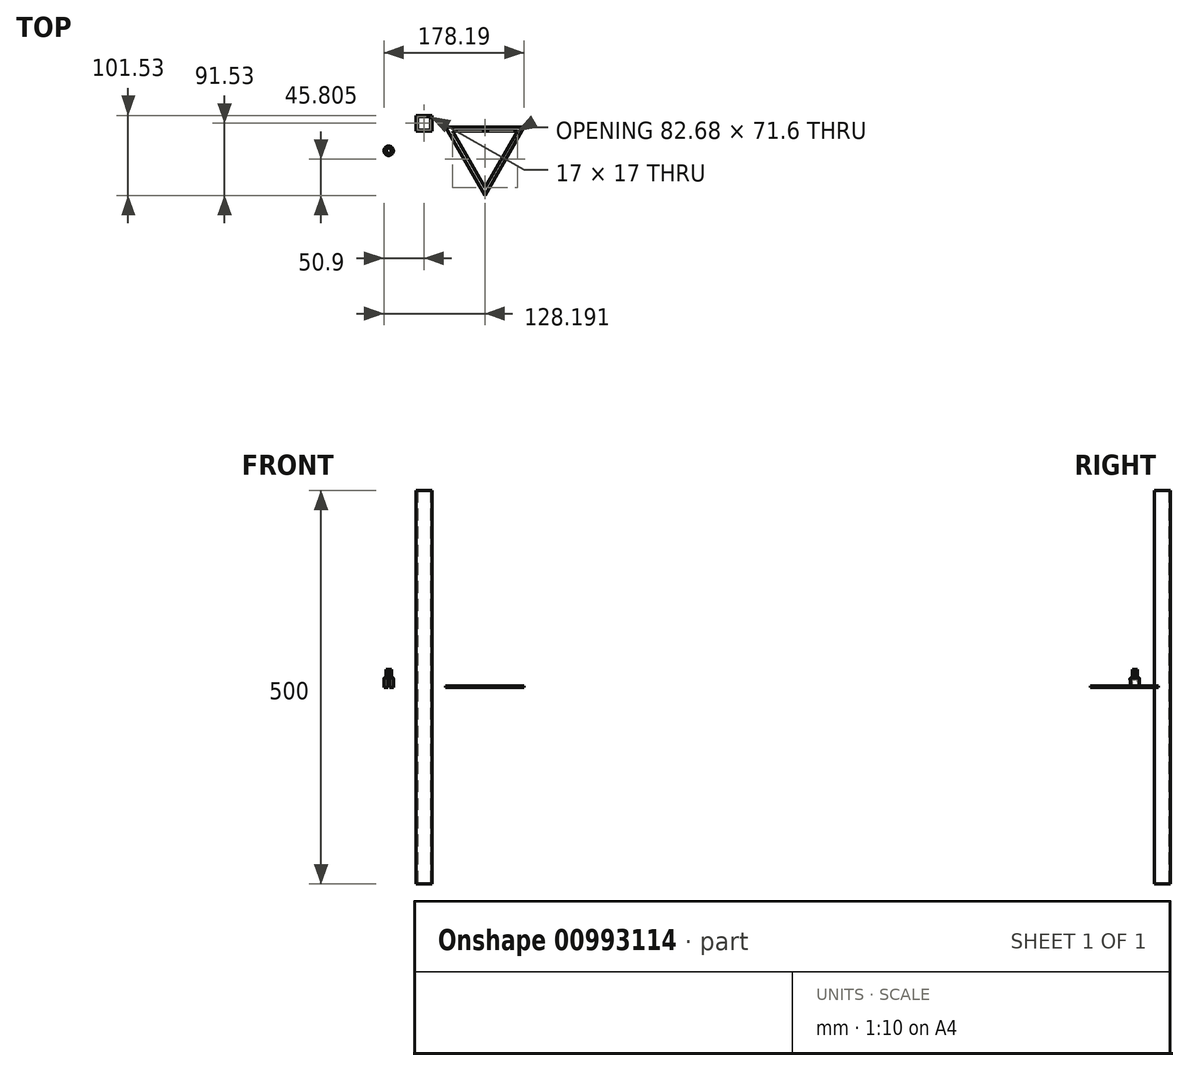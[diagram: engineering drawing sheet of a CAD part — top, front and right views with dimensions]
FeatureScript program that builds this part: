
annotation { "Feature Type Name" : "Feature", "Feature Type Description" : "" }
export const myFeature = defineFeature(function(context is Context, id is Id, definition is map)
    precondition{}
    {
        {
            var Q0;
            Q0=qCreatedBy(makeId("Top.planeOp"),FACE);
            var sketch = newSketch(context, id + "F0", { "sketchPlane" : qUnion([Q0])});
            skLineSegment(sketch, "E0.bottom", {"start": v(-10, 10) * mm, "end": v(10, 10) * mm});
            skLineSegment(sketch, "E0.top", {"start": v(-10, -10) * mm, "end": v(10, -10) * mm});
            skLineSegment(sketch, "E0.left", {"start": v(-10, 10) * mm, "end": v(-10, -10) * mm});
            skLineSegment(sketch, "E0.right", {"start": v(10, 10) * mm, "end": v(10, -10) * mm});
            skPoint(sketch, "E0.middle", {"position": v(0, 0) * mm});
            skLineSegment(sketch, "E1.0", {"start": v(-8.5, 8.5) * mm, "end": v(8.5, 8.5) * mm});
            skLineSegment(sketch, "E1.1", {"start": v(-8.5, 8.5) * mm, "end": v(-8.5, -8.5) * mm});
            skLineSegment(sketch, "E1.2", {"start": v(-8.5, -8.5) * mm, "end": v(8.5, -8.5) * mm});
            skLineSegment(sketch, "E1.3", {"start": v(8.5, 8.5) * mm, "end": v(8.5, -8.5) * mm});
            skLineSegment(sketch, "E2", {"start": v(27.3, -4.92) * mm, "end": v(127.3, -4.92) * mm});
            skLineSegment(sketch, "E3", {"start": v(127.3, -4.92) * mm, "end": v(77.3, -91.53) * mm});
            skLineSegment(sketch, "E4", {"start": v(77.3, -91.53) * mm, "end": v(27.3, -4.92) * mm});
            skLineSegment(sketch, "E5.0", {"start": v(77.3, -81.53) * mm, "end": v(35.95, -9.92) * mm});
            skLineSegment(sketch, "E5.1", {"start": v(118.63, -9.92) * mm, "end": v(77.3, -81.53) * mm});
            skLineSegment(sketch, "E5.2", {"start": v(35.95, -9.92) * mm, "end": v(118.63, -9.92) * mm});
            skSolve(sketch);
        }
        {
            var Q0;
            Q0=makeQuery(id+"F0.imprint","IMPRINT",FACE,{"disambiguationData":[TD([[makeQuery(id+"F0.imprint","IMPRINT",EDGE,{"derivedFrom":sQuery(id+"F0.wireOp",EDGE,"E0.bottom")}),-1.0]])]});
            extrude(context, id + "F1", {"entities" : qUnion([Q0]), "depth" : 500 * mm, "offsetDistance" : 25 * mm, "symmetric" : true});
        }
        {
            var Q0;
            Q0=makeQuery(id+"F0.imprint","IMPRINT",FACE,{"disambiguationData":[TD([[makeQuery(id+"F0.imprint","IMPRINT",EDGE,{"derivedFrom":sQuery(id+"F0.wireOp",EDGE,"E2")}),-1.0]])]});
            extrude(context, id + "F2", {"entities" : qUnion([Q0]), "depth" : 2 * mm, "offsetDistance" : 25 * mm});
        }
        {
            var Q0;
            Q0=qCreatedBy(makeId("Top.planeOp"),FACE);
            var sketch = newSketch(context, id + "F3", { "sketchPlane" : qUnion([Q0])});
            skCircle(sketch, "E6", {"center": v(-44.9, -34.92) * mm, "radius": 6 * mm});
            skCircle(sketch, "E7.0", {"center": v(-44.9, -34.92) * mm, "radius": 3.75 * mm});
            skSolve(sketch);
        }
        {
            var Q0;
            Q0 = qSketchRegion(id + "F3", true);
            var Q1;
            Q1=makeQuery(id+"F3.imprint","IMPRINT",FACE,{"disambiguationData":[TD([[makeQuery(id+"F3.imprint","IMPRINT",EDGE,{"derivedFrom":sQuery(id+"F3.wireOp",EDGE,"E7.0")}),1.0]])]});
            extrude(context, id + "F4", {"entities" : qUnion([Q0, Q1]), "depth" : 12 * mm, "offsetDistance" : 25 * mm});
        }
        {
            var Q0;
            Q0=makeQuery(id+"F3.imprint","IMPRINT",FACE,{"disambiguationData":[TD([[makeQuery(id+"F3.imprint","IMPRINT",EDGE,{"derivedFrom":sQuery(id+"F3.wireOp",EDGE,"E7.0")}),1.0]])]});
            extrude(context, id + "F5", {"entities" : qUnion([Q0]), "operationType" : NewBodyOperationType.REMOVE, "depth" : 9.7 * mm, "offsetDistance" : 25 * mm});
        }
        {
            var Q0;
            Q0=makeQuery(id+"F4.opExtrude","CAP_FACE",FACE,{"disambiguationData":[OSD([sQuery(id+"F3.wireOp",EDGE,"E6")])],"isStart":false});
            var sketch = newSketch(context, id + "F6", { "sketchPlane" : qUnion([Q0])});
            skPoint(sketch, "E8.0", {"position": v(-44.9, -34.92) * mm});
            skCircle(sketch, "E9.cCircle", {"center": v(-44.9, -34.92) * mm, "radius": 3.05 * mm, "construction": true});
            skLineSegment(sketch, "E9.0", {"start": v(-43.59, -31.66) * mm, "end": v(-41.41, -34.43) * mm});
            skLineSegment(sketch, "E9.1", {"start": v(-41.41, -34.43) * mm, "end": v(-42.73, -37.7) * mm});
            skLineSegment(sketch, "E9.2", {"start": v(-42.73, -37.7) * mm, "end": v(-46.22, -38.2) * mm});
            skLineSegment(sketch, "E9.3", {"start": v(-46.22, -38.2) * mm, "end": v(-48.39, -35.42) * mm});
            skLineSegment(sketch, "E9.4", {"start": v(-48.39, -35.42) * mm, "end": v(-47.07, -32.15) * mm});
            skLineSegment(sketch, "E9.5", {"start": v(-47.07, -32.15) * mm, "end": v(-43.59, -31.66) * mm});
            skPoint(sketch, "E9.0.midPoint", {"position": v(-42.5, -33.04) * mm});
            skSolve(sketch);
        }
        {
            var Q0;
            Q0=makeQuery(id+"F6.imprint","IMPRINT",FACE,{"disambiguationData":[TD([[makeQuery(id+"F6.imprint","IMPRINT",EDGE,{"derivedFrom":sQuery(id+"F6.wireOp",EDGE,"E9.0")}),-1.0]])]});
            extrude(context, id + "F7", {"entities" : qUnion([Q0]), "operationType" : NewBodyOperationType.ADD, "depth" : 10.5 * mm, "offsetDistance" : 25 * mm});
        }
        {
            var Q0;
            Q0=makeQuery(id+"F7.opExtrude","CAP_EDGE",EDGE,{"disambiguationData":[OSD([sQuery(id+"F6.wireOp",EDGE,"E9.2")])],"isStart":true});
            var Q1;
            Q1=makeQuery(id+"F7.opExtrude","CAP_EDGE",EDGE,{"disambiguationData":[OSD([sQuery(id+"F6.wireOp",EDGE,"E9.1")])],"isStart":true});
            var Q2;
            Q2=makeQuery(id+"F7.opExtrude","CAP_EDGE",EDGE,{"disambiguationData":[OSD([sQuery(id+"F6.wireOp",EDGE,"E9.0")])],"isStart":true});
            var Q3;
            Q3=makeQuery(id+"F7.opExtrude","CAP_EDGE",EDGE,{"disambiguationData":[OSD([sQuery(id+"F6.wireOp",EDGE,"E9.5")])],"isStart":true});
            var Q4;
            Q4=makeQuery(id+"F7.opExtrude","CAP_EDGE",EDGE,{"disambiguationData":[OSD([sQuery(id+"F6.wireOp",EDGE,"E9.4")])],"isStart":true});
            var Q5;
            Q5=makeQuery(id+"F7.opExtrude","CAP_EDGE",EDGE,{"disambiguationData":[OSD([sQuery(id+"F6.wireOp",EDGE,"E9.3")])],"isStart":true});
            var Q6;
            Q6=makeQuery(id+"F4.opExtrude","CAP_EDGE",EDGE,{"disambiguationData":[OSD([sQuery(id+"F3.wireOp",EDGE,"E6")])],"isStart":false});
            fillet(context, id + "F8", {"entities" : qUnion([Q0, Q1, Q2, Q3, Q4, Q5, Q6]), "radius" : .8 * mm, "tangentPropagation" : true, "allowEdgeOverflow" : false});
        }
        {
            var Q0;
            Q0=makeQuery(id+"F3.imprint","IMPRINT",FACE,{"disambiguationData":[TD([[makeQuery(id+"F3.imprint","IMPRINT",EDGE,{"derivedFrom":sQuery(id+"F3.wireOp",EDGE,"E6")}),1.0]])]});
            var sketch = newSketch(context, id + "F9", { "sketchPlane" : qUnion([Q0])});
            skPoint(sketch, "E10.0", {"position": v(-44.9, -34.92) * mm});
            skLineSegment(sketch, "E11.bottom", {"start": v(-43.9, -23.08) * mm, "end": v(-45.9, -23.08) * mm});
            skLineSegment(sketch, "E11.top", {"start": v(-43.9, -46.77) * mm, "end": v(-45.9, -46.77) * mm});
            skLineSegment(sketch, "E11.left", {"start": v(-43.9, -23.08) * mm, "end": v(-43.9, -46.77) * mm});
            skLineSegment(sketch, "E11.right", {"start": v(-45.9, -23.08) * mm, "end": v(-45.9, -46.77) * mm});
            skSolve(sketch);
        }
        {
            var Q0;
            Q0 = qSketchRegion(id + "F9", true);
            var Q1;
            {var subQ0=sQuery(id+"F9.wireOp",EDGE,"E11.bottom");Q1=makeQuery(id+"F9.imprint","IMPRINT",FACE,{"disambiguationData":[TD([[makeQuery(id+"F9.imprint","IMPRINT",EDGE,{"derivedFrom":subQ0}),1.0]])]});}
            extrude(context, id + "F10", {"entities" : qUnion([Q0, Q1]), "operationType" : NewBodyOperationType.REMOVE, "depth" : 9.5 * mm, "offsetDistance" : 25 * mm});
        }
        {
            var Q0;
            Q0=makeQuery(id+"F5.boolean.opBoolean","COPY",EDGE,{"derivedFrom":makeQuery(id+"F5.opExtrude","CAP_EDGE",EDGE,{"disambiguationData":[OSD([sQuery(id+"F3.wireOp",EDGE,"E7.0")])],"isStart":false})});
            fillet(context, id + "F11", {"entities" : qUnion([Q0]), "radius" : 3 * mm, "tangentPropagation" : true, "rho" : .8, "crossSection" : FilletCrossSection.CONIC, "allowEdgeOverflow" : false});
        }
    });
